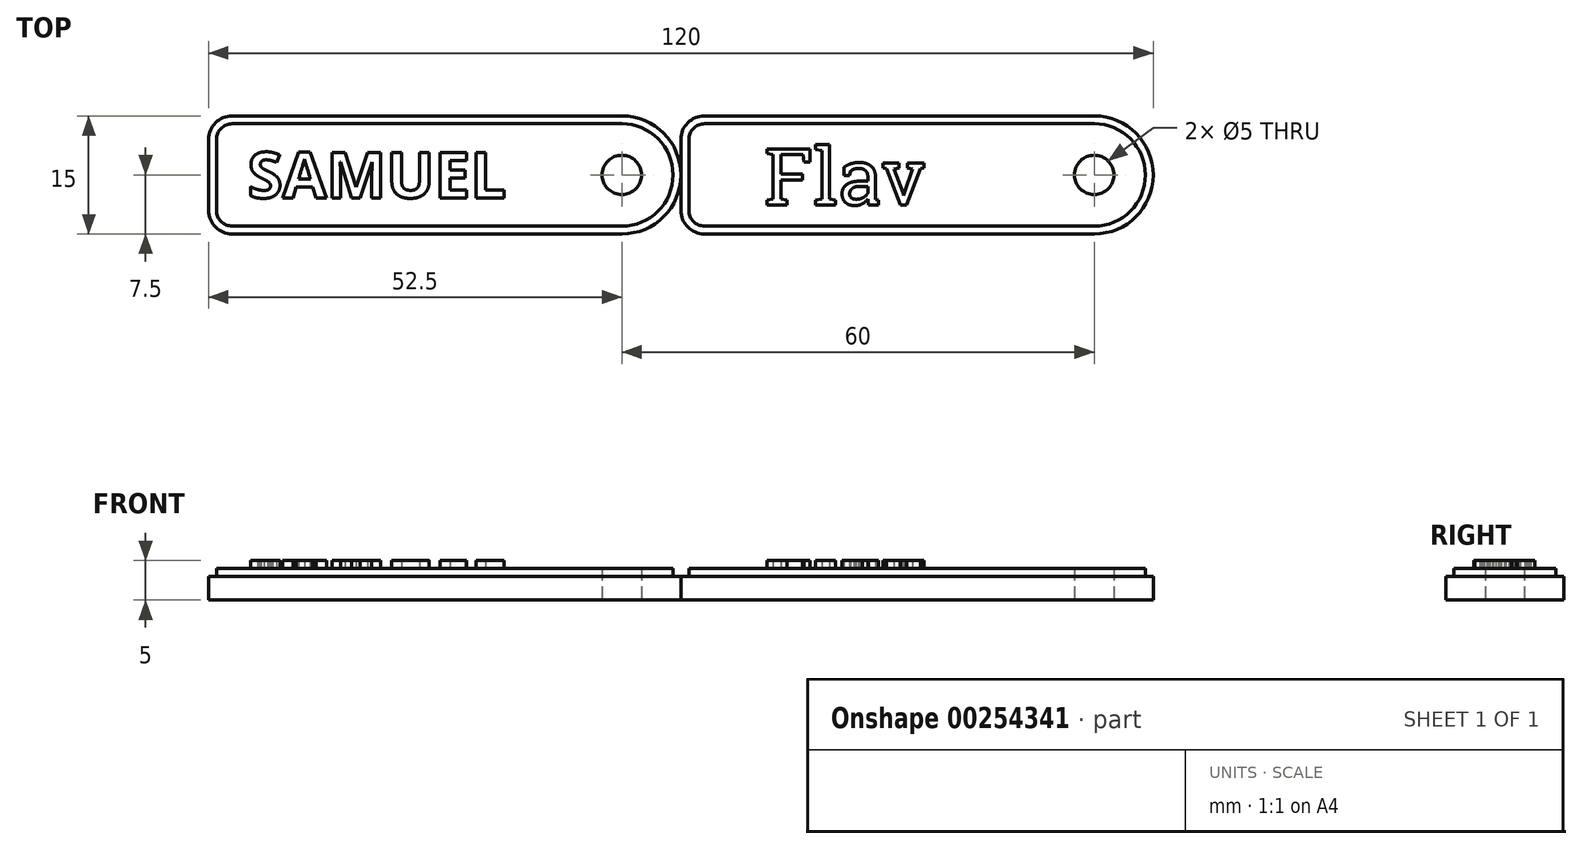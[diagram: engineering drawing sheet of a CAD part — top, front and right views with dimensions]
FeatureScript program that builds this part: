
annotation { "Feature Type Name" : "Feature", "Feature Type Description" : "" }
export const myFeature = defineFeature(function(context is Context, id is Id, definition is map)
    precondition{}
    {
        {
            var Q0;
            Q0=qCreatedBy(makeId("Top.planeOp"),FACE);
            var sketch = newSketch(context, id + "F0", { "sketchPlane" : qUnion([Q0])});
            skLineSegment(sketch, "E0.bottom", {"start": v(3, 7.5) * mm, "end": v(52.5, 7.5) * mm});
            skLineSegment(sketch, "E0.top", {"start": v(3, -7.5) * mm, "end": v(52.5, -7.5) * mm});
            skLineSegment(sketch, "E0.left", {"start": v(0, 4.5) * mm, "end": v(0, -4.5) * mm});
            skArc(sketch, "E1", {"start": v(52.5, -7.5) * mm, "mid": v(60, 0) * mm, "end": v(52.5, 7.5) * mm});
            skCircle(sketch, "E2", {"center": v(52.5, 0) * mm, "radius": 2.5 * mm});
            skPoint(sketch, "E3.visualSharp", {"position": v(0, 7.5) * mm});
            skArc(sketch, "E3.filletArc", {"start": v(3, 7.5) * mm, "mid": v(0.88, 6.62) * mm, "end": v(0, 4.5) * mm});
            skPoint(sketch, "E4.visualSharp", {"position": v(0, -7.5) * mm});
            skArc(sketch, "E4.filletArc", {"start": v(0, -4.5) * mm, "mid": v(0.88, -6.62) * mm, "end": v(3, -7.5) * mm});
            skLineSegment(sketch, "E5.0", {"start": v(3, 6.5) * mm, "end": v(52.5, 6.5) * mm});
            skLineSegment(sketch, "E5.1", {"start": v(1, 4.5) * mm, "end": v(1, -4.5) * mm});
            skArc(sketch, "E5.2", {"start": v(1, -4.5) * mm, "mid": v(1.59, -5.91) * mm, "end": v(3, -6.5) * mm});
            skArc(sketch, "E5.3", {"start": v(3, 6.5) * mm, "mid": v(1.59, 5.91) * mm, "end": v(1, 4.5) * mm});
            skLineSegment(sketch, "E5.4", {"start": v(3, -6.5) * mm, "end": v(52.5, -6.5) * mm});
            skArc(sketch, "E5.5", {"start": v(52.5, -6.5) * mm, "mid": v(59, 0) * mm, "end": v(52.5, 6.5) * mm});
            skSolve(sketch);
        }
        {
            var Q0;
            Q0 = qSketchRegion(id + "F0", true);
            extrude(context, id + "F1", {"entities" : qUnion([Q0]), "depth" : 3 * mm});
        }
        {
            var Q0;
            Q0=qCreatedBy(makeId("Top.planeOp"),FACE);
            var sketch = newSketch(context, id + "F2", { "sketchPlane" : qUnion([Q0])});
            skLineSegment(sketch, "E6.bottom", {"start": v(-57, -7.5) * mm, "end": v(-7.5, -7.5) * mm});
            skLineSegment(sketch, "E6.top", {"start": v(-57, 7.5) * mm, "end": v(-7.5, 7.5) * mm});
            skLineSegment(sketch, "E6.left", {"start": v(-60, 4.5) * mm, "end": v(-60, -4.5) * mm});
            skArc(sketch, "E7", {"start": v(-7.5, 7.5) * mm, "mid": v(0, 0) * mm, "end": v(-7.5, -7.5) * mm});
            skCircle(sketch, "E8", {"center": v(-7.5, 0) * mm, "radius": 2.5 * mm});
            skPoint(sketch, "E9.visualSharp", {"position": v(-60, -7.5) * mm});
            skPoint(sketch, "E10.visualSharp", {"position": v(-60, 7.5) * mm});
            skLineSegment(sketch, "E11", {"start": v(-57, 7.5) * mm, "end": v(-57, 7.5) * mm});
            skArc(sketch, "E12.filletArc", {"start": v(-57, 7.5) * mm, "mid": v(-59.12, 6.62) * mm, "end": v(-60, 4.5) * mm});
            skArc(sketch, "E13.filletArc", {"start": v(-60, -4.5) * mm, "mid": v(-59.12, -6.62) * mm, "end": v(-57, -7.5) * mm});
            skArc(sketch, "E14.0", {"start": v(-57, 6.5) * mm, "mid": v(-58.41, 5.91) * mm, "end": v(-59, 4.5) * mm});
            skArc(sketch, "E14.1", {"start": v(-7.5, 6.5) * mm, "mid": v(-1, 0) * mm, "end": v(-7.5, -6.5) * mm});
            skLineSegment(sketch, "E14.2", {"start": v(-57, -6.5) * mm, "end": v(-7.5, -6.5) * mm});
            skLineSegment(sketch, "E14.3", {"start": v(-57, 6.5) * mm, "end": v(-7.5, 6.5) * mm});
            skArc(sketch, "E14.4", {"start": v(-59, -4.5) * mm, "mid": v(-58.41, -5.91) * mm, "end": v(-57, -6.5) * mm});
            skLineSegment(sketch, "E14.5", {"start": v(-59, 4.5) * mm, "end": v(-59, -4.5) * mm});
            skSolve(sketch);
        }
        {
            var Q0;
            Q0=makeQuery(id+"F2.imprint","IMPRINT",FACE,{"disambiguationData":[TD([[makeQuery(id+"F2.imprint","IMPRINT",EDGE,{"derivedFrom":sQuery(id+"F2.wireOp",EDGE,"E6.bottom")}),1.0]])]});
            extrude(context, id + "F3", {"entities" : qUnion([Q0]), "operationType" : NewBodyOperationType.ADD, "depth" : 3 * mm});
        }
        {
            var Q0;
            Q0=makeQuery(id+"F2.imprint","IMPRINT",FACE,{"disambiguationData":[TD([[makeQuery(id+"F2.imprint","IMPRINT",EDGE,{"derivedFrom":sQuery(id+"F2.wireOp",EDGE,"E8")}),-1.0]])]});
            extrude(context, id + "F4", {"entities" : qUnion([Q0]), "operationType" : NewBodyOperationType.ADD, "depth" : 4 * mm});
        }
        {
            var Q0;
            Q0=qCreatedBy(makeId("Top.planeOp"),FACE);
            var sketch = newSketch(context, id + "F5", { "sketchPlane" : qUnion([Q0])});
            skText(sketch, "E15", { "text": "SAMUEL", "fontName": "OpenSans-Bold.ttf"});
            skPoint(sketch, "E16.end.orphan", {"position": v(-7.37, -3.7) * mm});
            skPoint(sketch, "E17.start.orphan", {"position": v(-7.37, -5.56) * mm});
            skPoint(sketch, "E18", {"position": v(-44.71, -5.21) * mm});
            skPoint(sketch, "E19", {"position": v(-27.33, -5.2) * mm});
            const initialGuessF5  = {"E15": [-0.05506, -0.00291, 1, 0, 0.00582]};
            skSetInitialGuess(sketch, initialGuessF5);
            skSolve(sketch);
        }
        {
            var Q0;
            Q0 = qSketchRegion(id + "F5", true);
            extrude(context, id + "F6", {"entities" : qUnion([Q0]), "operationType" : NewBodyOperationType.ADD, "depth" : 5 * mm});
        }
        {
            var Q0;
            Q0=qCreatedBy(makeId("Top.planeOp"),FACE);
            var sketch = newSketch(context, id + "F7", { "sketchPlane" : qUnion([Q0])});
            skText(sketch, "E20", { "text": "Flav", "fontName": "RobotoSlab-Regular.ttf"});
            const initialGuessF7  = {"E20": [0.01058, -0.0038, 1, 0, 0.00721]};
            skSetInitialGuess(sketch, initialGuessF7);
            skSolve(sketch);
        }
        {
            var Q0;
            Q0=makeQuery(id+"F0.imprint","IMPRINT",FACE,{"disambiguationData":[TD([[makeQuery(id+"F0.imprint","IMPRINT",EDGE,{"derivedFrom":sQuery(id+"F0.wireOp",EDGE,"E2")}),-1.0]])]});
            extrude(context, id + "F8", {"entities" : qUnion([Q0]), "operationType" : NewBodyOperationType.ADD, "depth" : 4 * mm});
        }
        {
            var Q0;
            Q0 = qSketchRegion(id + "F7", true);
            extrude(context, id + "F9", {"entities" : qUnion([Q0]), "operationType" : NewBodyOperationType.ADD, "depth" : 5 * mm});
        }
    });
